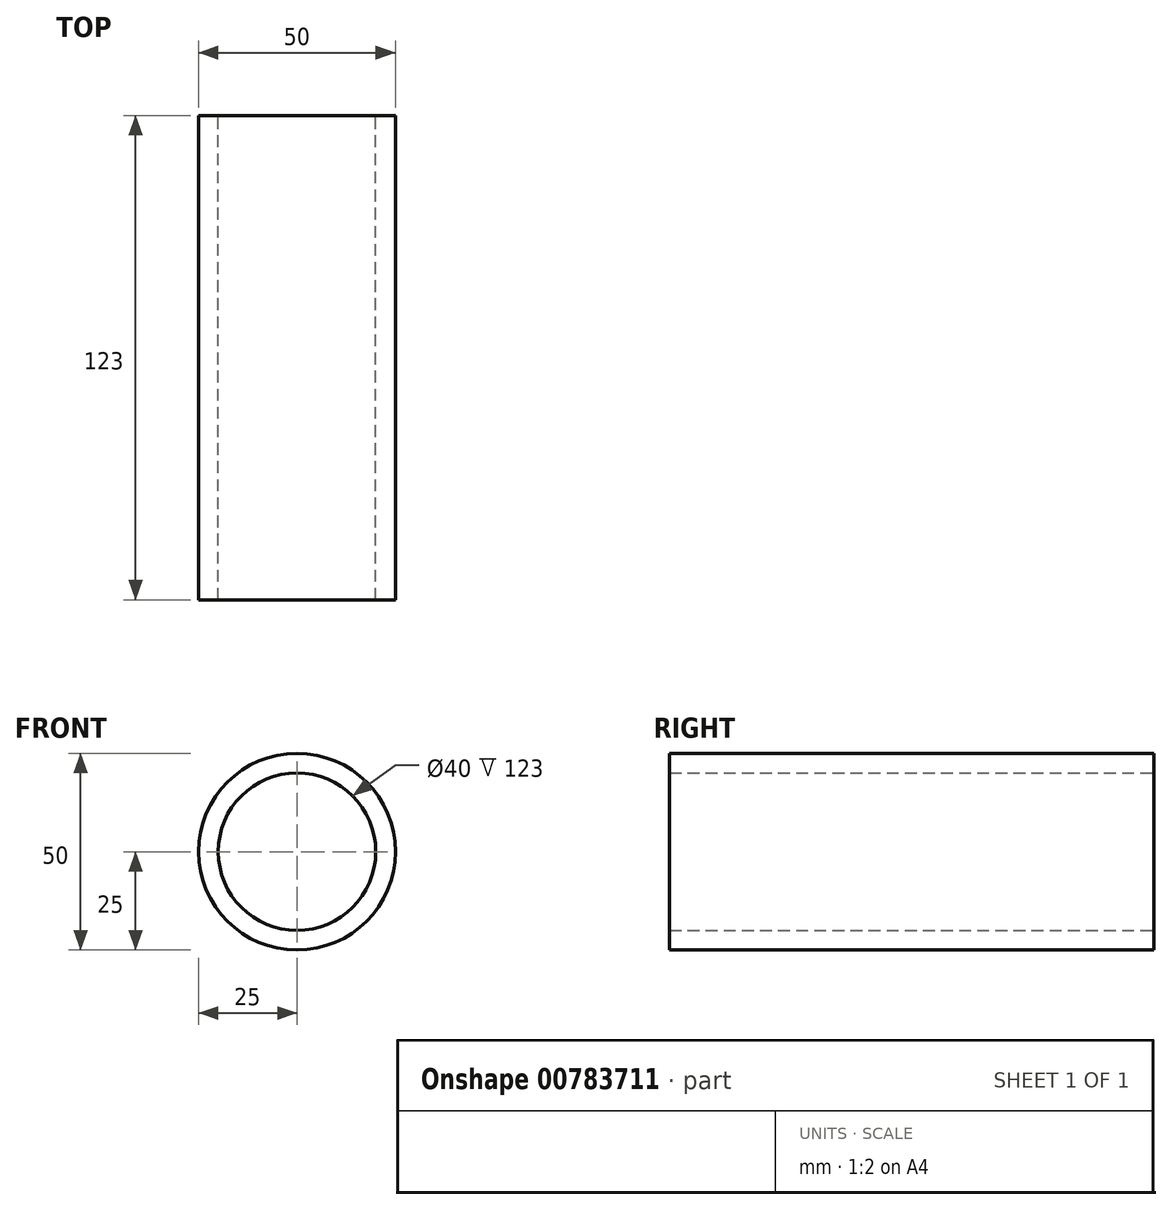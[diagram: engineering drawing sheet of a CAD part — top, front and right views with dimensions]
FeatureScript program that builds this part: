
annotation { "Feature Type Name" : "Feature", "Feature Type Description" : "" }
export const myFeature = defineFeature(function(context is Context, id is Id, definition is map)
    precondition{}
    {
        {
            var Q0;
            Q0=qCreatedBy(makeId("Front.planeOp"),FACE);
            var sketch = newSketch(context, id + "F0", { "sketchPlane" : qUnion([Q0])});
            skCircle(sketch, "E0", {"center": v(0, 0) * mm, "radius": 25 * mm});
            skCircle(sketch, "E1", {"center": v(0, 0) * mm, "radius": 20 * mm});
            skSolve(sketch);
        }
        {
            var Q0;
            Q0=makeQuery(id+"F0.imprint","IMPRINT",FACE,{"disambiguationData":[TD([[makeQuery(id+"F0.imprint","IMPRINT",EDGE,{"derivedFrom":sQuery(id+"F0.wireOp",EDGE,"E0")}),1.0]])]});
            extrude(context, id + "F1", {"entities" : qUnion([Q0]), "depth" : 123 * mm, "offsetDistance" : 25 * mm});
        }
    });
